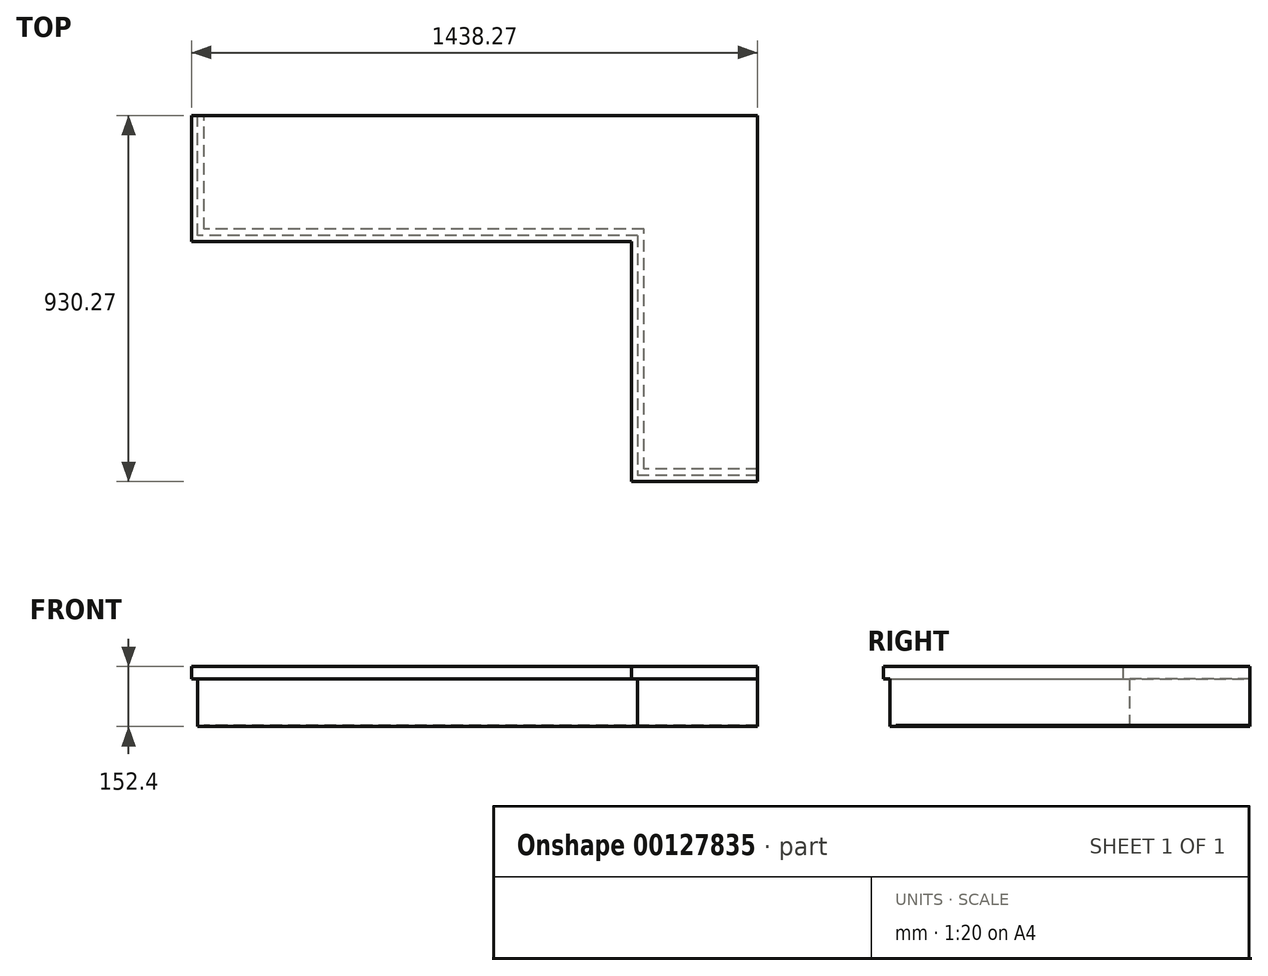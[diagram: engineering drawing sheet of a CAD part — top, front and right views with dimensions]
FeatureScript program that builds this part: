
annotation { "Feature Type Name" : "Feature", "Feature Type Description" : "" }
export const myFeature = defineFeature(function(context is Context, id is Id, definition is map)
    precondition{}
    {
        {
            var Q0;
            Q0=qCreatedBy(makeId("Top.planeOp"),FACE);
            var sketch = newSketch(context, id + "F0", { "sketchPlane" : qUnion([Q0])});
            skLineSegment(sketch, "E0", {"start": v(-1422.4, 0) * mm, "end": v(0, 0) * mm});
            skLineSegment(sketch, "E1", {"start": v(0, 0) * mm, "end": v(0, 0) * mm});
            skLineSegment(sketch, "E2", {"start": v(0, -914.4) * mm, "end": v(0, 0) * mm});
            skLineSegment(sketch, "E3", {"start": v(0, -914.4) * mm, "end": v(-304.8, -914.4) * mm});
            skLineSegment(sketch, "E4", {"start": v(-304.8, -914.4) * mm, "end": v(-304.8, -914.4) * mm});
            skLineSegment(sketch, "E5", {"start": v(-304.8, -304.8) * mm, "end": v(-304.8, -914.4) * mm});
            skLineSegment(sketch, "E6", {"start": v(-304.8, -304.8) * mm, "end": v(-1422.4, -304.8) * mm});
            skLineSegment(sketch, "E7", {"start": v(-1422.4, -304.8) * mm, "end": v(-1422.4, 0) * mm});
            skLineSegment(sketch, "E8", {"start": v(-1422.4, 0) * mm, "end": v(-1422.4, 0) * mm});
            skSolve(sketch);
        }
        {
            var Q0;
            Q0 = qSketchRegion(id + "F0", true);
            extrude(context, id + "F4", {"entities" : qUnion([Q0]), "oppositeDirection" : true, "depth" : 152.4 * mm});
        }
        {
            var Q0;
            Q0=makeQuery(id+"F4.opExtrude","CAP_FACE",FACE,{"disambiguationData":[OSD([sQuery(id+"F0.wireOp",EDGE,"E0"),sQuery(id+"F0.wireOp",EDGE,"E2"),sQuery(id+"F0.wireOp",EDGE,"E3"),sQuery(id+"F0.wireOp",EDGE,"E5"),sQuery(id+"F0.wireOp",EDGE,"E6"),sQuery(id+"F0.wireOp",EDGE,"E7")])],"isStart":true});
            var sketch = newSketch(context, id + "F5", { "sketchPlane" : qUnion([Q0])});
            skLineSegment(sketch, "E9", {"start": v(0, 0) * mm, "end": v(0, 0) * mm});
            skLineSegment(sketch, "E10", {"start": v(0, 0) * mm, "end": v(0, -930.28) * mm});
            skLineSegment(sketch, "E11", {"start": v(0, -930.28) * mm, "end": v(-320.68, -930.28) * mm});
            skLineSegment(sketch, "E12", {"start": v(-320.68, -930.28) * mm, "end": v(-320.68, -320.67) * mm});
            skLineSegment(sketch, "E13", {"start": v(-320.68, -320.67) * mm, "end": v(-1438.28, -320.68) * mm});
            skLineSegment(sketch, "E14", {"start": v(-1438.28, -320.68) * mm, "end": v(-1438.28, 0) * mm});
            skLineSegment(sketch, "E15", {"start": v(-1438.28, 0) * mm, "end": v(0, 0) * mm});
            skSolve(sketch);
        }
        {
            var Q0;
            Q0 = qSketchRegion(id + "F5", true);
            extrude(context, id + "F1", {"entities" : qUnion([Q0]), "operationType" : NewBodyOperationType.ADD, "oppositeDirection" : true, "depth" : 31.75 * mm});
        }
        {
            var Q0;
            Q0=makeQuery(id+"F4.opExtrude","CAP_FACE",FACE,{"disambiguationData":[OSD([sQuery(id+"F0.wireOp",EDGE,"E0"),sQuery(id+"F0.wireOp",EDGE,"E2"),sQuery(id+"F0.wireOp",EDGE,"E3"),sQuery(id+"F0.wireOp",EDGE,"E5"),sQuery(id+"F0.wireOp",EDGE,"E6"),sQuery(id+"F0.wireOp",EDGE,"E7")])],"isStart":false});
            var sketch = newSketch(context, id + "F2", { "sketchPlane" : qUnion([Q0])});
            skLineSegment(sketch, "E16.0", {"start": v(-1406.53, 288.93) * mm, "end": v(-1406.53, 15.88) * mm});
            skLineSegment(sketch, "E16.1", {"start": v(-15.88, 15.88) * mm, "end": v(-15.88, 898.53) * mm, "construction": true});
            skLineSegment(sketch, "E16.2", {"start": v(-15.88, 898.53) * mm, "end": v(-288.93, 898.53) * mm});
            skLineSegment(sketch, "E16.3", {"start": v(-1406.53, 15.88) * mm, "end": v(-15.88, 15.88) * mm, "construction": true});
            skLineSegment(sketch, "E16.4", {"start": v(-288.93, 898.53) * mm, "end": v(-288.93, 288.92) * mm});
            skLineSegment(sketch, "E16.5", {"start": v(-288.93, 288.92) * mm, "end": v(-1406.53, 288.93) * mm});
            skLineSegment(sketch, "E17", {"start": v(-1406.53, 15.88) * mm, "end": v(-1406.53, 0) * mm});
            skLineSegment(sketch, "E18", {"start": v(-1406.53, 0) * mm, "end": v(0, 0) * mm});
            skLineSegment(sketch, "E19", {"start": v(0, 0) * mm, "end": v(0, 898.53) * mm});
            skLineSegment(sketch, "E20", {"start": v(0, 898.53) * mm, "end": v(-15.88, 898.53) * mm});
            skSolve(sketch);
        }
        {
            var Q0;
            Q0 = qSketchRegion(id + "F2", true);
            extrude(context, id + "F3", {"entities" : qUnion([Q0]), "operationType" : NewBodyOperationType.REMOVE, "oppositeDirection" : true, "depth" : 3.17 * mm});
        }
    });
